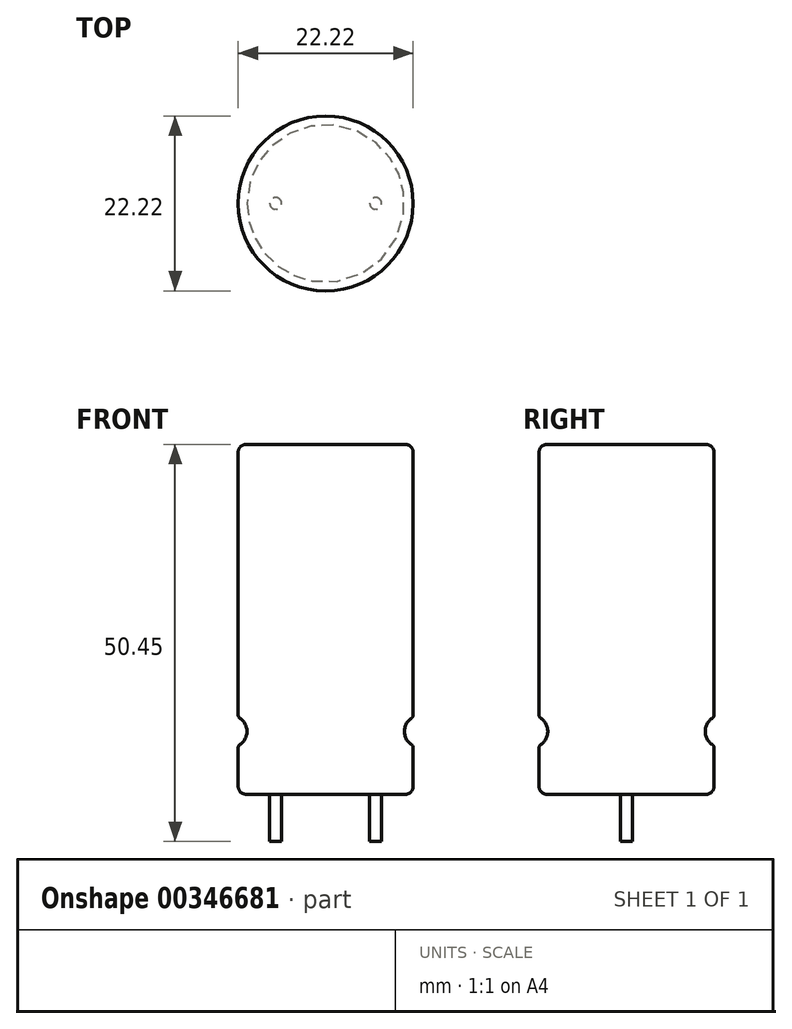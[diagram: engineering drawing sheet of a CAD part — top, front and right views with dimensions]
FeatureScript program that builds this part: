
annotation { "Feature Type Name" : "Feature", "Feature Type Description" : "" }
export const myFeature = defineFeature(function(context is Context, id is Id, definition is map)
    precondition{}
    {
        {
            var Q0;
            Q0=qCreatedBy(makeId("Front.planeOp"),FACE);
            var sketch = newSketch(context, id + "F0", { "sketchPlane" : qUnion([Q0])});
            skLineSegment(sketch, "E0", {"start": v(0, 0) * mm, "end": v(11.11, 0) * mm});
            skLineSegment(sketch, "E1", {"start": v(11.11, 0) * mm, "end": v(11.11, 6.2) * mm});
            skLineSegment(sketch, "E2", {"start": v(0, 0) * mm, "end": v(0, 44.45) * mm});
            skLineSegment(sketch, "E3", {"start": v(0, 44.45) * mm, "end": v(11.11, 44.45) * mm});
            skLineSegment(sketch, "E4", {"start": v(11.11, 44.45) * mm, "end": v(11.11, 9.78) * mm});
            skArc(sketch, "E5", {"start": v(11.11, 9.78) * mm, "mid": v(10, 8) * mm, "end": v(11.11, 6.2) * mm});
            skSolve(sketch);
        }
        {
            var Q0;
            Q0=qSketchRegion(id+"F0",true);
            var Q1;
            Q1=sQuery(id+"F0.wireOp",EDGE,"E2");
            revolve(context, id + "F1", {"entities" : qUnion([Q0]), "axis" : qUnion([Q1]), "revolveType" : RevolveType.FULL});
        }
        {
            var Q0;
            Q0=makeQuery(id+"F1.opRevolve","SWEPT_EDGE",EDGE,{"disambiguationData":[OSD([sQuery(id+"F0.wireOp",EDGE,"E3"),sQuery(id+"F0.wireOp",EDGE,"E4")])]});
            fillet(context, id + "F2", {"entities" : qUnion([Q0]), "radius" : 1 * mm, "tangentPropagation" : true, "allowEdgeOverflow" : false});
        }
        {
            var Q0;
            Q0=makeQuery(id+"F1.opRevolve","SWEPT_FACE",FACE,{"disambiguationData":[OSD([sQuery(id+"F0.wireOp",EDGE,"E4")])]});
            var Q1;
            Q1=makeQuery(id+"F1.opRevolve","SWEPT_EDGE",EDGE,{"disambiguationData":[OSD([sQuery(id+"F0.wireOp",EDGE,"E1"),sQuery(id+"F0.wireOp",EDGE,"E5")])]});
            fillet(context, id + "F3", {"entities" : qUnion([Q0, Q1]), "radius" : .5 * mm, "tangentPropagation" : true, "allowEdgeOverflow" : false});
        }
        {
            var Q0;
            Q0=makeQuery(id+"F1.opRevolve","SWEPT_EDGE",EDGE,{"disambiguationData":[OSD([sQuery(id+"F0.wireOp",EDGE,"E0"),sQuery(id+"F0.wireOp",EDGE,"E1")])]});
            fillet(context, id + "F4", {"entities" : qUnion([Q0]), "radius" : 1 * mm, "tangentPropagation" : true, "allowEdgeOverflow" : false});
        }
        {
            var Q0;
            Q0=makeQuery(id+"F1.opRevolve","SWEPT_FACE",FACE,{"disambiguationData":[OSD([sQuery(id+"F0.wireOp",EDGE,"E0")])]});
            var sketch = newSketch(context, id + "F5", { "sketchPlane" : qUnion([Q0])});
            skCircle(sketch, "E6", {"center": v(-6.35, 0) * mm, "radius": 0.75 * mm});
            skCircle(sketch, "E7", {"center": v(6.35, 0) * mm, "radius": 0.75 * mm});
            skSolve(sketch);
        }
        {
            var Q0;
            Q0=qSketchRegion(id+"F5",true);
            extrude(context, id + "F6", {"entities" : qUnion([Q0]), "operationType" : NewBodyOperationType.ADD, "depth" : 6 * mm});
        }
    });
